# Revit family: Haworth_XSeries_VerticalStorage
name_source: partatom
category: Furniture Systems
units: mm (PartAtom-declared; Revit-internal decimal feet)

## family parameters
Always vertical = Yes
Cut with Voids When Loaded = No
OmniClass Number = 23.40.70.14.64.21
OmniClass Title = Systems Furniture
Part Type = Normal
Room Calculation Point = No
Round Connector Dimension = Use Diameter
Shared = No
Work Plane-Based = No

## types (3) — shared parameters
Actual Depth = 14 1/4"
Actual Height = 34 1/4"
Actual Width = 72"
Assembly Code = E2020200
Custom Size = No
Description = Haworth XSeries Vertical Storage Unit
Door 1 Right Edge = 1/8"
Door Height = 17"
Manufacturer = Haworth
Max. Width = 72"
Min. Width = 48"
Model = JUFL-3372
Revision Number = 4
Size = Verify Final Dim. w/ Haworth
Standard Widths = 48, 60, 66, 72 in.
Sustainability Info = https://www.haworth.com
URL = http://www.haworth.com
URL - Product = https://www.haworth.com
Warranty = https://cdn.shopify.com
Width = 72"

## per-type parameters (varying)
| type | Center Vertical | Divider Half | Door 2 Left Edge | Door Width | Door2 | Flip Door | Open | Sliding Door |
| 14d 34h 72w - Flipper Doors | Yes | 3/4" | 1/8" | 35 5/8" | Yes | Yes | No | No |
| 14d 34h 72w - Sliding Door | No | 1/16" | 8" | 36" | Yes | No | No | Yes |
| 14d 34h 72w - Open | No | 1/16" | 1/8" | 36" | No | No | Yes | No |

## geometry (parser evidence)
native form markers: Sweep x7
no freeform markers — native parametric forms only
